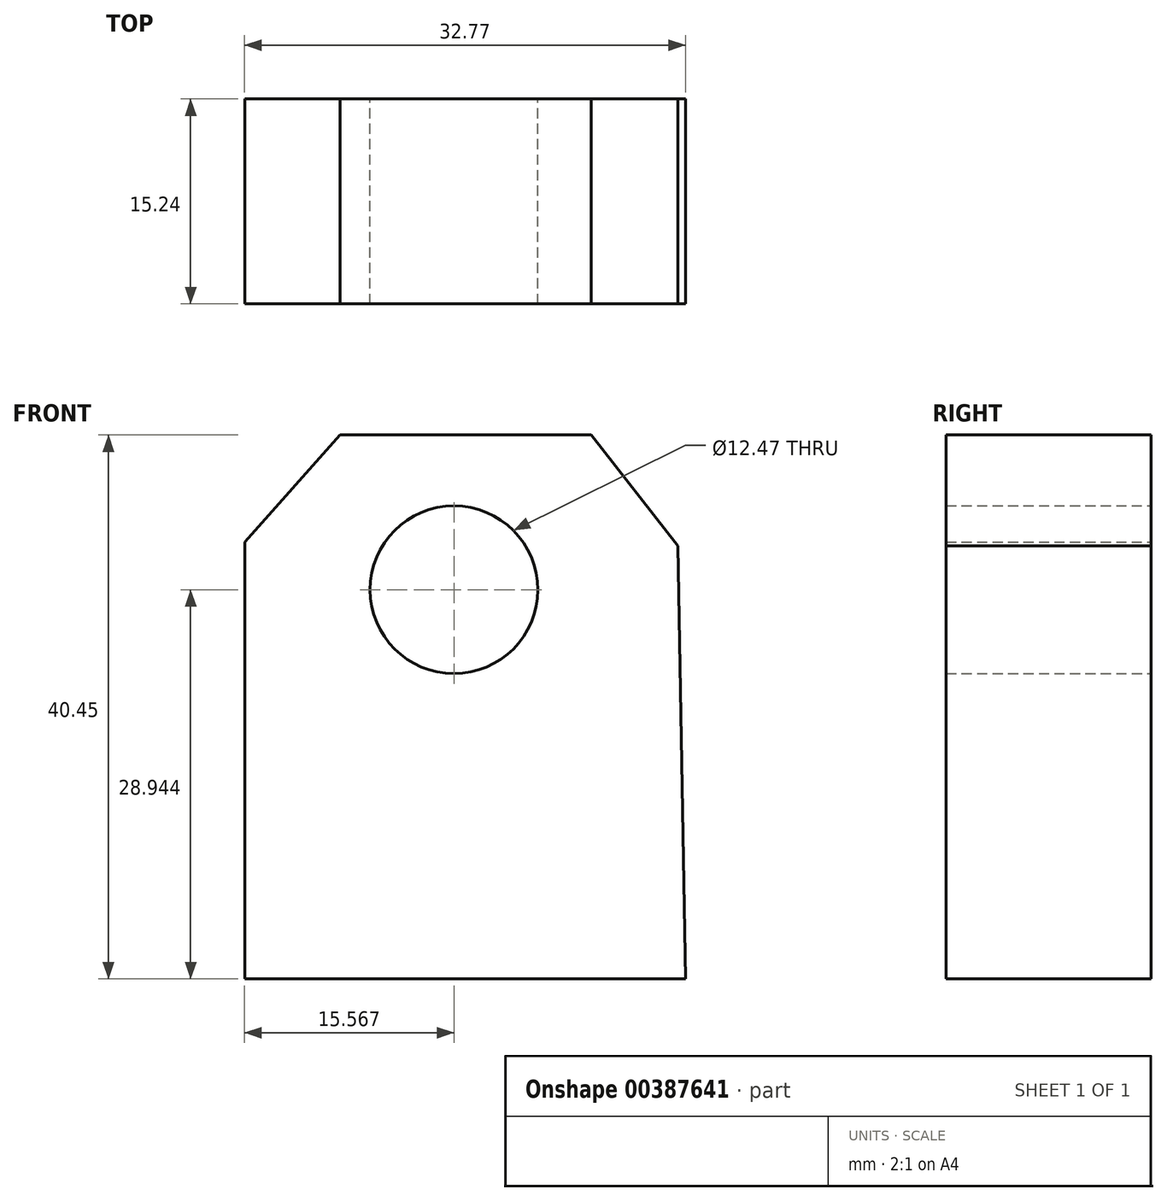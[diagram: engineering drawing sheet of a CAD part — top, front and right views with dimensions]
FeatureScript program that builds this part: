
annotation { "Feature Type Name" : "Feature", "Feature Type Description" : "" }
export const myFeature = defineFeature(function(context is Context, id is Id, definition is map)
    precondition{}
    {
        {
            var Q0;
            Q0=qCreatedBy(makeId("Front.planeOp"),FACE);
            var sketch = newSketch(context, id + "F0", { "sketchPlane" : qUnion([Q0])});
            skLineSegment(sketch, "E0", {"start": v(-15.84, 27.9) * mm, "end": v(2.82, 27.9) * mm});
            skLineSegment(sketch, "E1", {"start": v(2.82, 27.9) * mm, "end": v(9.28, 19.66) * mm});
            skLineSegment(sketch, "E2", {"start": v(-15.84, 27.9) * mm, "end": v(-22.94, 19.93) * mm});
            skPoint(sketch, "E3.end.orphan", {"position": v(11.2, -5.73) * mm});
            skPoint(sketch, "E3.start.orphan", {"position": v(-22.94, -5.73) * mm});
            skLineSegment(sketch, "E4", {"start": v(-22.94, 19.93) * mm, "end": v(-22.94, -12.56) * mm});
            skLineSegment(sketch, "E5", {"start": v(-22.94, -12.56) * mm, "end": v(9.83, -12.56) * mm});
            skLineSegment(sketch, "E6", {"start": v(9.28, 19.66) * mm, "end": v(9.83, -12.56) * mm});
            skCircle(sketch, "E7", {"center": v(-7.37, 16.38) * mm, "radius": 6.23 * mm});
            skSolve(sketch);
        }
        {
            var Q0;
            Q0=qSketchRegion(id+"F0",true);
            extrude(context, id + "F1", {"entities" : qUnion([Q0]), "depth" : 15.24 * mm});
        }
    });
